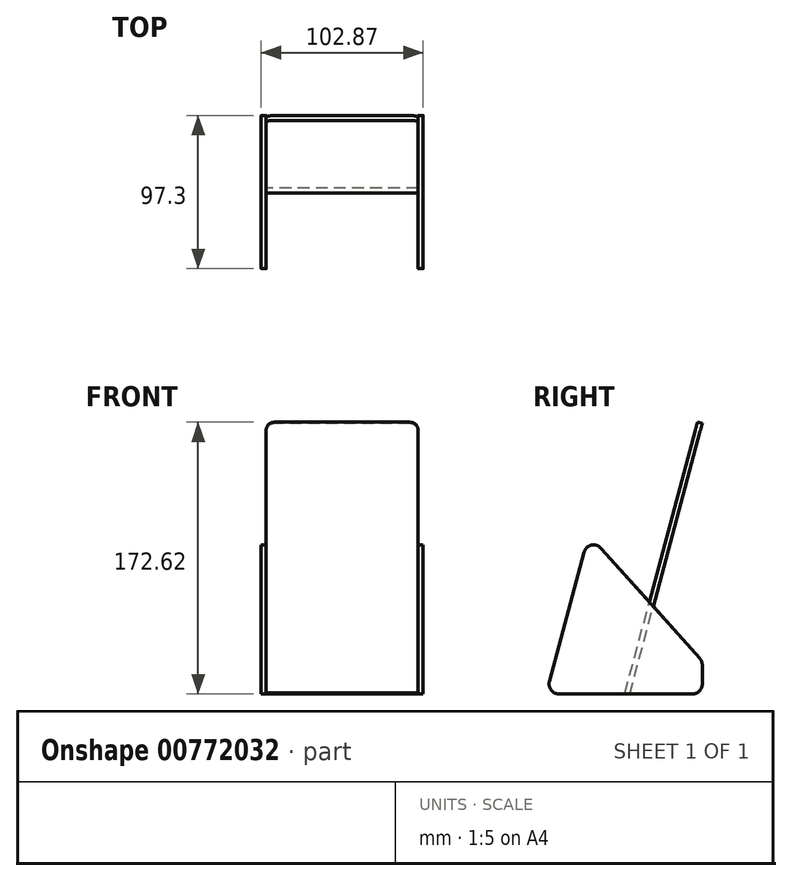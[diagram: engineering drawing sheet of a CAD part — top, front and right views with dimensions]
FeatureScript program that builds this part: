
annotation { "Feature Type Name" : "Feature", "Feature Type Description" : "" }
export const myFeature = defineFeature(function(context is Context, id is Id, definition is map)
    precondition{}
    {
        {
            var Q0;
            Q0=qCreatedBy(makeId("Right.planeOp"),FACE);
            var sketch = newSketch(context, id + "F0", { "sketchPlane" : qUnion([Q0])});
            skLineSegment(sketch, "E0", {"start": v(0, 0) * mm, "end": v(46.02, 171.74) * mm});
            skLineSegment(sketch, "E1", {"start": v(0, 0) * mm, "end": v(-3.07, 0.82) * mm});
            skLineSegment(sketch, "E2", {"start": v(-3.07, 0.82) * mm, "end": v(42.97, 172.62) * mm});
            skLineSegment(sketch, "E3", {"start": v(42.97, 172.62) * mm, "end": v(46.02, 171.74) * mm});
            skSolve(sketch);
        }
        {
            var Q0;
            Q0 = qSketchRegion(id + "F0", true);
            extrude(context, id + "F1", {"entities" : qUnion([Q0]), "depth" : 96.52 * mm, "offsetDistance" : 25.4 * mm});
        }
        {
            var Q0;
            Q0=qCreatedBy(makeId("Right.planeOp"),FACE);
            var sketch = newSketch(context, id + "F2", { "sketchPlane" : qUnion([Q0])});
            skLineSegment(sketch, "E4", {"start": v(0, 0) * mm, "end": v(39.67, 0) * mm});
            skLineSegment(sketch, "E5", {"start": v(46.02, 6.35) * mm, "end": v(46.02, 18.36) * mm});
            skLineSegment(sketch, "E6", {"start": v(44.4, 22.6) * mm, "end": v(-18.23, 92.59) * mm});
            skLineSegment(sketch, "E7", {"start": v(-29.1, 90) * mm, "end": v(-49.64, 13.3) * mm});
            skLineSegment(sketch, "E8", {"start": v(-49.64, 13.3) * mm, "end": v(0, 0) * mm});
            skPoint(sketch, "E9.visualSharp", {"position": v(46.02, 20.78) * mm});
            skArc(sketch, "E9.filletArc", {"start": v(46.02, 18.36) * mm, "mid": v(45.6, 20.62) * mm, "end": v(44.4, 22.6) * mm});
            skPoint(sketch, "E10.visualSharp", {"position": v(46.02, 0) * mm});
            skArc(sketch, "E10.filletArc", {"start": v(39.67, 0) * mm, "mid": v(44.16, 1.86) * mm, "end": v(46.02, 6.35) * mm});
            skPoint(sketch, "E11.visualSharp", {"position": v(-26.05, 101.33) * mm});
            skArc(sketch, "E11.filletArc", {"start": v(-18.23, 92.59) * mm, "mid": v(-24.43, 94.53) * mm, "end": v(-29.1, 90) * mm});
            skLineSegment(sketch, "E12", {"start": v(-49.64, 13.3) * mm, "end": v(-51.06, 8) * mm});
            skLineSegment(sketch, "E13", {"start": v(-44.93, 0) * mm, "end": v(0, 0) * mm});
            skPoint(sketch, "E14.visualSharp", {"position": v(-53.2, 0) * mm});
            skArc(sketch, "E14.filletArc", {"start": v(-51.06, 8) * mm, "mid": v(-49.97, 2.48) * mm, "end": v(-44.93, 0) * mm});
            skSolve(sketch);
        }
        {
            var Q0;
            Q0 = qSketchRegion(id + "F2", true);
            extrude(context, id + "F3", {"entities" : qUnion([Q0]), "oppositeDirection" : true, "depth" : 3.17 * mm, "offsetDistance" : 25.4 * mm});
        }
        {
            var Q0;
            Q0=makeQuery(id+"F1.opExtrude","SWEPT_FACE",FACE,{"disambiguationData":[OSD([sQuery(id+"F0.wireOp",EDGE,"E2")])]});
            var sketch = newSketch(context, id + "F4", { "sketchPlane" : qUnion([Q0])});
            skLineSegment(sketch, "E15", {"start": v(48.26, 177.85) * mm, "end": v(48.26, 0) * mm, "construction": true});
            skSolve(sketch);
        }
        {
            var Q0;
            Q0=makeQuery(id+"F1.opExtrude","SWEPT_FACE",FACE,{"disambiguationData":[OSD([sQuery(id+"F0.wireOp",EDGE,"E1")])]});
            var sketch = newSketch(context, id + "F5", { "sketchPlane" : qUnion([Q0])});
            skLineSegment(sketch, "E16", {"start": v(48.26, 3.17) * mm, "end": v(48.26, 0) * mm, "construction": true});
            skSolve(sketch);
        }
        {
            var Q0;
            Q0=makeQuery(id+"F1.opExtrude","SWEPT_EDGE",EDGE,{"disambiguationData":[OSD([sQuery(id+"F0.wireOp",EDGE,"E2"),sQuery(id+"F0.wireOp",EDGE,"E3")])]});
            cPoint(context, id + "F6", {"entities" : qUnion([Q0]), "parameter" : 0.5});
        }
        {
            var Q0;
            Q0 = qCreatedBy(id + "F6" ,VERTEX);
            var Q1;
            Q1=sQuery(id+"F4.wireOp",VERTEX,"E15.end");
            var Q2;
            Q2=sQuery(id+"F5.wireOp",VERTEX,"E16.end");
            cPlane(context, id + "F7", {"entities" : qUnion([Q0, Q1, Q2]), "cplaneType" : CPlaneType.THREE_POINT, "offset" : 25.4 * mm, "width" : 152.4 * mm, "height" : 152.4 * mm});
        }
        {
            var Q0;
            Q0=makeQuery(id+"F3.opExtrude","SWEPT_BODY",BODY,{"disambiguationData":[OSD([sQuery(id+"F2.wireOp",EDGE,"E4"),sQuery(id+"F2.wireOp",EDGE,"E5"),sQuery(id+"F2.wireOp",EDGE,"E6"),sQuery(id+"F2.wireOp",EDGE,"E7"),sQuery(id+"F2.wireOp",EDGE,"E9.filletArc"),sQuery(id+"F2.wireOp",EDGE,"E10.filletArc"),sQuery(id+"F2.wireOp",EDGE,"E11.filletArc"),sQuery(id+"F2.wireOp",EDGE,"E12"),sQuery(id+"F2.wireOp",EDGE,"E13"),sQuery(id+"F2.wireOp",EDGE,"E14.filletArc")])]});
            var Q1;
            Q1=qCreatedBy(id+"F7.planeOp",FACE);
            mirror(context, id + "F8", {"entities" : qUnion([Q0]), "mirrorPlane" : qUnion([Q1])});
        }
        {
            var Q0;
            Q0=makeQuery(id+"F1.opExtrude","CAP_EDGE",EDGE,{"disambiguationData":[OSD([sQuery(id+"F0.wireOp",EDGE,"E3")])],"isStart":true});
            var Q1;
            Q1=makeQuery(id+"F1.opExtrude","CAP_EDGE",EDGE,{"disambiguationData":[OSD([sQuery(id+"F0.wireOp",EDGE,"E3")])],"isStart":false});
            fillet(context, id + "F9", {"entities" : qUnion([Q0, Q1]), "radius" : 5.08 * mm, "tangentPropagation" : true, "allowEdgeOverflow" : false});
        }
    });
